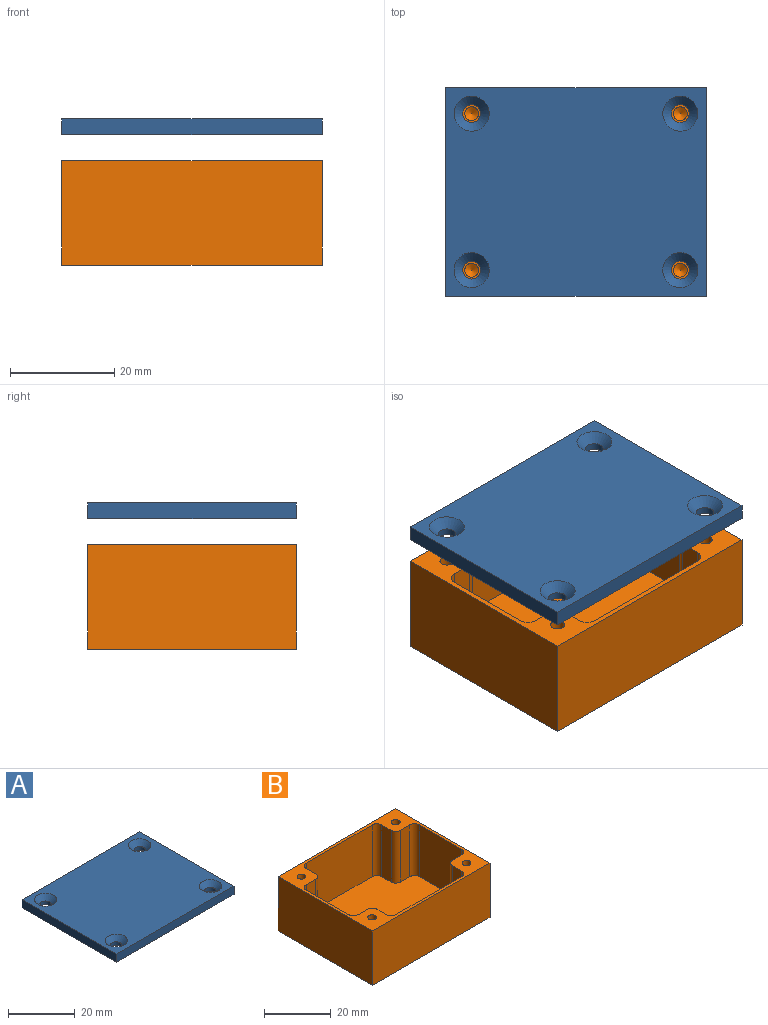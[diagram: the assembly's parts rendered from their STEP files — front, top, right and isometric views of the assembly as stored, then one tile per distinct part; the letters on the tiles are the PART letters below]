
ASSEMBLY  parts=2 mates=1
PART A: 14 faces, bbox 50x40x3 mm
  f0: plane 40x3mm, normal (-1,0,0), area 120mm2, adj f1,f3,f4,f5
  f1: plane 50x3mm, normal (0,-1,0), area 150mm2, adj f0,f2,f4,f5
  f2: plane 40x3mm, normal (1,0,0), area 120mm2, adj f1,f3,f4,f5
  f3: plane 50x3mm, normal (0,1,0), area 150mm2, adj f0,f2,f4,f5
  f4: plane 50x40mm, normal (0,0,1), area 1858.1mm2, adj f0,f1,f2,f3,f7,f9,f11,f13
  f5: plane 50x40mm, normal (0,0,-1), area 1963.7mm2, adj f0,f1,f2,f3,f6,f8,f10,f12
  f6: cylinder r=1.7mm len=3.4mm, axis (0,0,1), area 14.3mm2, adj f5,f7
  f7: cone r=1.7mm half-angle=45deg, axis (0,0,1), area 37.3mm2, adj f4,f6
  f8: cylinder r=1.7mm len=3.4mm, axis (0,0,1), area 14.3mm2, adj f5,f9
  f9: cone r=1.7mm half-angle=45deg, axis (0,0,1), area 37.3mm2, adj f4,f8
  f10: cylinder r=1.7mm len=3.4mm, axis (0,0,1), area 14.3mm2, adj f5,f11
  f11: cone r=1.7mm half-angle=45deg, axis (0,0,1), area 37.3mm2, adj f4,f10
  f12: cylinder r=1.7mm len=3.4mm, axis (0,0,1), area 14.3mm2, adj f5,f13
  f13: cone r=1.7mm half-angle=45deg, axis (0,0,1), area 37.3mm2, adj f4,f12
PART B: 39 faces, bbox 50x40x20 mm
  f0: plane 48x38mm, normal (0,0,1), area 1564.6mm2, adj f1,f2,f3,f4,f11,f12,f13,f14
  f1: plane 28x19mm, normal (0,1,0), area 532mm2, adj f0,f5,f28,f32
  f2: plane 19x18mm, normal (-1,0,0), area 342mm2, adj f0,f5,f30,f33
  f3: plane 28x19mm, normal (0,-1,0), area 532mm2, adj f0,f5,f34,f38
  f4: plane 19x18mm, normal (1,0,0), area 342mm2, adj f0,f5,f27,f36
  f5: plane 50x40mm, normal (0,0,1), area 413.4mm2, adj f1,f2,f3,f4,f6,f7,f8,f9
  f6: plane 40x20mm, normal (-1,0,0), area 800mm2, adj f5,f7,f9,f10
  f7: plane 50x20mm, normal (0,-1,0), area 1000mm2, adj f5,f6,f8,f10
  f8: plane 40x20mm, normal (1,0,0), area 800mm2, adj f5,f7,f9,f10
  f9: plane 50x20mm, normal (0,1,0), area 1000mm2, adj f5,f6,f8,f10
  f10: plane 50x40mm, normal (0,0,-1), area 2000mm2, adj f6,f7,f8,f9
  f11: plane 19x4mm, normal (0,-1,0), area 76mm2, adj f0,f5,f36,f37
  f12: plane 19x4mm, normal (1,0,0), area 76mm2, adj f0,f5,f37,f38
  f13: plane 19x4mm, normal (0,-1,0), area 76mm2, adj f0,f5,f33,f35
  f14: plane 19x4mm, normal (-1,0,0), area 76mm2, adj f0,f5,f34,f35
  f15: plane 19x4mm, normal (0,1,0), area 76mm2, adj f0,f5,f30,f31
  f16: plane 19x4mm, normal (-1,0,0), area 76mm2, adj f0,f5,f31,f32
  f17: plane 19x4mm, normal (0,1,0), area 76mm2, adj f0,f5,f27,f29
  f18: plane 19x4mm, normal (1,0,0), area 76mm2, adj f0,f5,f28,f29
  f19: cylinder r=1.32mm len=13.05mm, axis (0,0,1), area 108.6mm2, adj f5,f20
  f20: cone r=0mm half-angle=59deg, axis (0,0,1), area 6.4mm2, adj f19
  f21: cylinder r=1.32mm len=13.05mm, axis (0,0,1), area 108.6mm2, adj f5,f22
  f22: cone r=0mm half-angle=59deg, axis (0,0,1), area 6.4mm2, adj f21
  f23: cylinder r=1.32mm len=13.05mm, axis (0,0,1), area 108.6mm2, adj f5,f24
  f24: cone r=0mm half-angle=59deg, axis (0,0,1), area 6.4mm2, adj f23
  f25: cylinder r=1.32mm len=13.05mm, axis (0,0,1), area 108.6mm2, adj f5,f26
  f26: cone r=0mm half-angle=59deg, axis (0,0,1), area 6.4mm2, adj f25
  f27: cylinder r=2mm len=19mm, axis (0,0,-1), area 59.7mm2, adj f0,f4,f5,f17
  f28: cylinder r=2mm len=19mm, axis (0,0,-1), area 59.7mm2, adj f0,f1,f5,f18
  f29: cylinder r=2mm len=19mm, axis (0,0,1), area 59.7mm2, adj f0,f5,f17,f18
  f30: cylinder r=2mm len=19mm, axis (0,0,-1), area 59.7mm2, adj f0,f2,f5,f15
  f31: cylinder r=2mm len=19mm, axis (0,0,1), area 59.7mm2, adj f0,f5,f15,f16
  f32: cylinder r=2mm len=19mm, axis (0,0,1), area 59.7mm2, adj f0,f1,f5,f16
  f33: cylinder r=2mm len=19mm, axis (0,0,1), area 59.7mm2, adj f0,f2,f5,f13
  f34: cylinder r=2mm len=19mm, axis (0,0,1), area 59.7mm2, adj f0,f3,f5,f14
  f35: cylinder r=2mm len=19mm, axis (0,0,1), area 59.7mm2, adj f0,f5,f13,f14
  f36: cylinder r=2mm len=19mm, axis (0,0,1), area 59.7mm2, adj f0,f4,f5,f11
  f37: cylinder r=2mm len=19mm, axis (0,0,1), area 59.7mm2, adj f0,f5,f11,f12
  f38: cylinder r=2mm len=19mm, axis (0,0,-1), area 59.7mm2, adj f0,f3,f5,f12
PLACE A t=(0,0,5.01)mm
PLACE B at identity fixed
MATE slider A.f5 <-> B.f5  axis (0,0,1) through (0,0,25.01)mm
